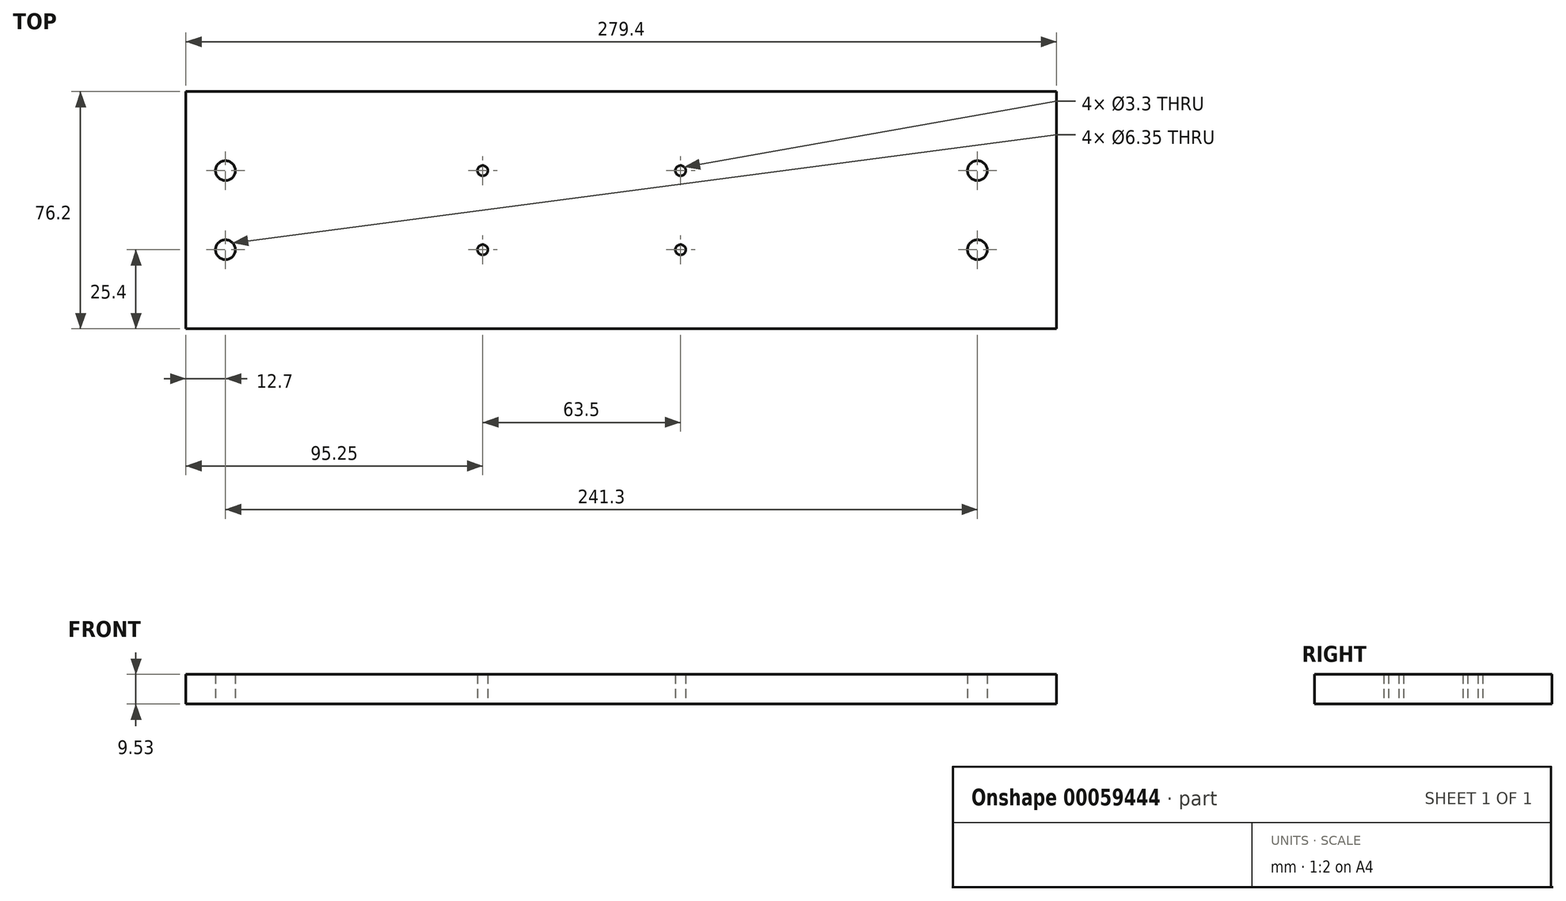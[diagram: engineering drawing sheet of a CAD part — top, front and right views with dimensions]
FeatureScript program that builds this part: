
annotation { "Feature Type Name" : "Feature", "Feature Type Description" : "" }
export const myFeature = defineFeature(function(context is Context, id is Id, definition is map)
    precondition{}
    {
        {
            var Q0;
            Q0=qCreatedBy(makeId("Top.planeOp"),FACE);
            var sketch = newSketch(context, id + "F0", { "sketchPlane" : qUnion([Q0])});
            skLineSegment(sketch, "E0.bottom", {"start": v(0, 0) * mm, "end": v(279.4, 0) * mm});
            skLineSegment(sketch, "E0.top", {"start": v(0, 76.2) * mm, "end": v(279.4, 76.2) * mm});
            skLineSegment(sketch, "E0.left", {"start": v(0, 0) * mm, "end": v(0, 76.2) * mm});
            skLineSegment(sketch, "E0.right", {"start": v(279.4, 0) * mm, "end": v(279.4, 76.2) * mm});
            skCircle(sketch, "E1", {"center": v(12.7, 50.8) * mm, "radius": 3.18 * mm});
            skCircle(sketch, "E2", {"center": v(12.7, 25.4) * mm, "radius": 3.18 * mm});
            skCircle(sketch, "E3", {"center": v(254, 50.8) * mm, "radius": 3.17 * mm});
            skCircle(sketch, "E4", {"center": v(254, 25.4) * mm, "radius": 3.18 * mm});
            skCircle(sketch, "E5", {"center": v(158.75, 50.8) * mm, "radius": 1.65 * mm});
            skCircle(sketch, "E6", {"center": v(95.25, 50.8) * mm, "radius": 1.65 * mm});
            skCircle(sketch, "E7", {"center": v(95.25, 25.4) * mm, "radius": 1.65 * mm});
            skCircle(sketch, "E8", {"center": v(158.75, 25.4) * mm, "radius": 1.65 * mm});
            skSolve(sketch);
        }
        {
            var Q0;
            Q0=makeQuery(id+"F0.imprint","IMPRINT",FACE,{"disambiguationData":[TD([[makeQuery(id+"F0.imprint","IMPRINT",EDGE,{"derivedFrom":sQuery(id+"F0.wireOp",EDGE,"E0.bottom")}),1.0]])]});
            extrude(context, id + "F1", {"entities" : qUnion([Q0]), "depth" : 9.52 * mm});
        }
    });
